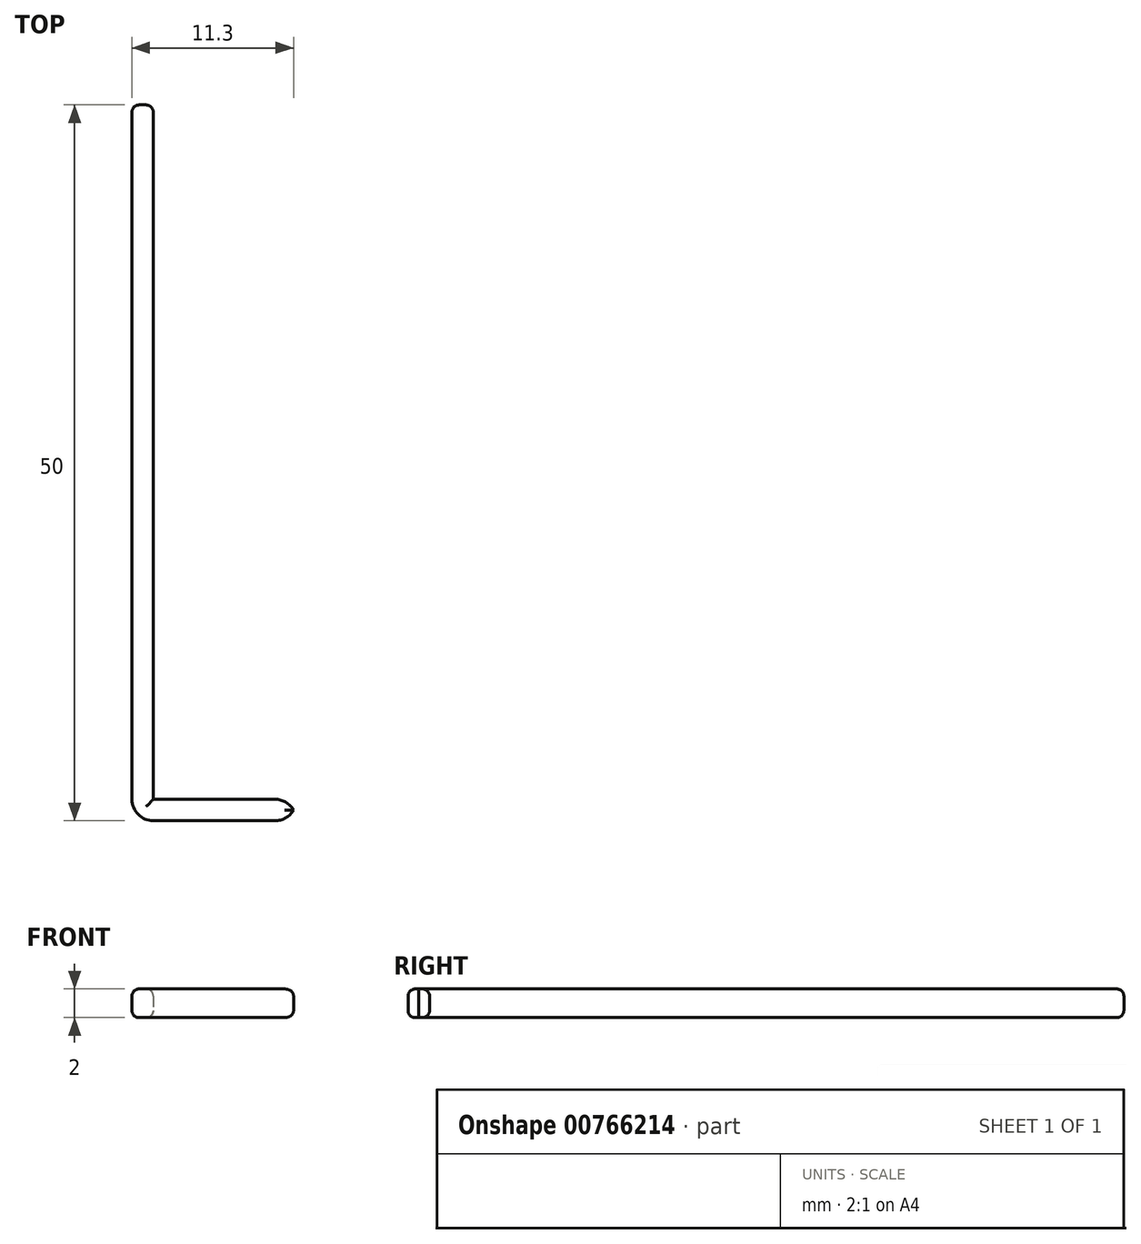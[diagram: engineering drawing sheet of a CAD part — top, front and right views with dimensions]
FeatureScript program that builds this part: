
annotation { "Feature Type Name" : "Feature", "Feature Type Description" : "" }
export const myFeature = defineFeature(function(context is Context, id is Id, definition is map)
    precondition{}
    {
        {
            var Q0;
            Q0=qCreatedBy(makeId("Top.planeOp"),FACE);
            var sketch = newSketch(context, id + "F0", { "sketchPlane" : qUnion([Q0])});
            skLineSegment(sketch, "E0", {"start": v(0, 0) * mm, "end": v(0, -50) * mm});
            skLineSegment(sketch, "E1", {"start": v(0, -50) * mm, "end": v(11.5, -50) * mm});
            skLineSegment(sketch, "E2", {"start": v(11.5, -50) * mm, "end": v(11.5, -48.5) * mm});
            skLineSegment(sketch, "E3", {"start": v(11.5, -48.5) * mm, "end": v(1.5, -48.5) * mm});
            skLineSegment(sketch, "E4", {"start": v(1.5, -48.5) * mm, "end": v(1.5, 0) * mm});
            skLineSegment(sketch, "E5", {"start": v(1.5, 0) * mm, "end": v(0, 0) * mm});
            skSolve(sketch);
        }
        {
            var Q0;
            Q0 = qSketchRegion(id + "F0", true);
            extrude(context, id + "F1", {"entities" : qUnion([Q0]), "depth" : 2 * mm, "offsetDistance" : 25 * mm});
        }
        {
            var Q0;
            Q0=makeQuery(id+"F1.opExtrude","SWEPT_EDGE",EDGE,{"disambiguationData":[OSD([sQuery(id+"F0.wireOp",EDGE,"E1"),sQuery(id+"F0.wireOp",EDGE,"E2")])]});
            var Q1;
            Q1=makeQuery(id+"F1.opExtrude","SWEPT_EDGE",EDGE,{"disambiguationData":[OSD([sQuery(id+"F0.wireOp",EDGE,"E0"),sQuery(id+"F0.wireOp",EDGE,"E1")])]});
            var Q2;
            Q2=makeQuery(id+"F1.opExtrude","SWEPT_EDGE",EDGE,{"disambiguationData":[OSD([sQuery(id+"F0.wireOp",EDGE,"E2"),sQuery(id+"F0.wireOp",EDGE,"E3")])]});
            fillet(context, id + "F2", {"entities" : qUnion([Q0, Q1, Q2]), "radius" : 1.5 * mm, "tangentPropagation" : true, "allowEdgeOverflow" : false});
        }
        {
            var Q0;
            Q0=makeQuery(id+"F1.opExtrude","CAP_EDGE",EDGE,{"disambiguationData":[OSD([sQuery(id+"F0.wireOp",EDGE,"E0")])],"isStart":false});
            var Q1;
            Q1=makeQuery(id+"F1.opExtrude","CAP_EDGE",EDGE,{"disambiguationData":[OSD([sQuery(id+"F0.wireOp",EDGE,"E0")])],"isStart":true});
            var Q2;
            Q2=makeQuery(id+"F1.opExtrude","CAP_EDGE",EDGE,{"disambiguationData":[OSD([sQuery(id+"F0.wireOp",EDGE,"E4")])],"isStart":true});
            var Q3;
            Q3=makeQuery(id+"F1.opExtrude","CAP_EDGE",EDGE,{"disambiguationData":[OSD([sQuery(id+"F0.wireOp",EDGE,"E4")])],"isStart":false});
            var Q4;
            Q4=makeQuery(id+"F1.opExtrude","SWEPT_FACE",FACE,{"disambiguationData":[OSD([sQuery(id+"F0.wireOp",EDGE,"E5")])]});
            var Q5;
            Q5=makeQuery(id+"F1.opExtrude","CAP_FACE",FACE,{"disambiguationData":[OSD([sQuery(id+"F0.wireOp",EDGE,"E0"),sQuery(id+"F0.wireOp",EDGE,"E1"),sQuery(id+"F0.wireOp",EDGE,"E2"),sQuery(id+"F0.wireOp",EDGE,"E3"),sQuery(id+"F0.wireOp",EDGE,"E4"),sQuery(id+"F0.wireOp",EDGE,"E5")])],"isStart":true});
            var Q6;
            Q6=makeQuery(id+"F1.opExtrude","CAP_FACE",FACE,{"disambiguationData":[OSD([sQuery(id+"F0.wireOp",EDGE,"E0"),sQuery(id+"F0.wireOp",EDGE,"E1"),sQuery(id+"F0.wireOp",EDGE,"E2"),sQuery(id+"F0.wireOp",EDGE,"E3"),sQuery(id+"F0.wireOp",EDGE,"E4"),sQuery(id+"F0.wireOp",EDGE,"E5")])],"isStart":false});
            fillet(context, id + "F3", {"entities" : qUnion([Q0, Q1, Q2, Q3, Q4, Q5, Q6]), "radius" : 0.5 * mm, "tangentPropagation" : true, "allowEdgeOverflow" : false});
        }
    });
